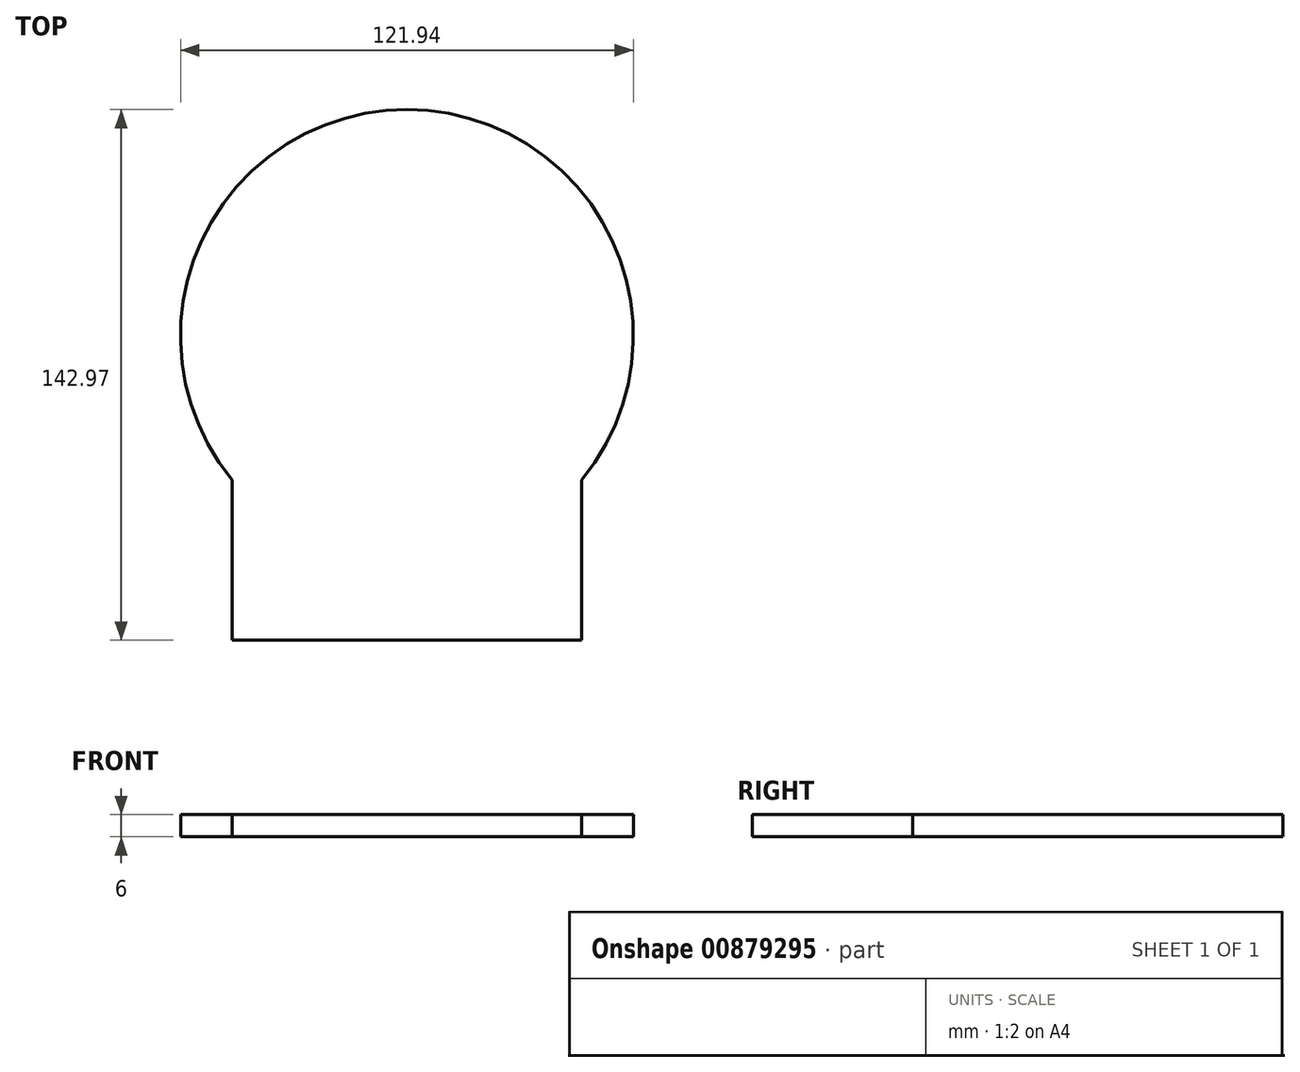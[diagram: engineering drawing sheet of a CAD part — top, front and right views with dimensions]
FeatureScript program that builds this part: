
annotation { "Feature Type Name" : "Feature", "Feature Type Description" : "" }
export const myFeature = defineFeature(function(context is Context, id is Id, definition is map)
    precondition{}
    {
        {
            var Q0;
            Q0=qCreatedBy(makeId("Top.planeOp"),FACE);
            var sketch = newSketch(context, id + "F0", { "sketchPlane" : qUnion([Q0])});
            skArc(sketch, "E0.0", {"start": v(-100, 44.36) * mm, "mid": v(-50, 149.43) * mm, "end": v(0, 44.36) * mm});
            skLineSegment(sketch, "E1.0", {"start": v(-100, 44.36) * mm, "end": v(-100, 0) * mm});
            skLineSegment(sketch, "E2.0", {"start": v(-100, 0) * mm, "end": v(0, 0) * mm});
            skLineSegment(sketch, "E3.0", {"start": v(0, 44.36) * mm, "end": v(0, 0) * mm});
            skLineSegment(sketch, "E4.0", {"start": v(-3, 46.16) * mm, "end": v(-3, 3) * mm});
            skArc(sketch, "E5.0", {"start": v(-97, 46.16) * mm, "mid": v(-50, 145.97) * mm, "end": v(-3, 46.16) * mm});
            skLineSegment(sketch, "E6.0", {"start": v(-97, 46.16) * mm, "end": v(-97, 3) * mm});
            skLineSegment(sketch, "E7.0", {"start": v(-97, 3) * mm, "end": v(-3, 3) * mm});
            skSolve(sketch);
        }
        {
            var Q0;
            Q0=makeQuery(id+"F0.imprint","IMPRINT",FACE,{"disambiguationData":[TD([[makeQuery(id+"F0.imprint","IMPRINT",EDGE,{"derivedFrom":sQuery(id+"F0.wireOp",EDGE,"E4.0")}),-1.0]])]});
            var Q1;
            Q1=makeQuery(id+"F0.imprint","IMPRINT",FACE,{"disambiguationData":[TD([[makeQuery(id+"F0.imprint","IMPRINT",EDGE,{"derivedFrom":sQuery(id+"F0.wireOp",EDGE,"E0.0")}),-1.0]])]});
            extrude(context, id + "F1", {"entities" : qUnion([Q0, Q1]), "depth" : 3 * mm, "offsetDistance" : 25 * mm});
        }
        {
            var Q0;
            Q0=makeQuery(id+"F0.imprint","IMPRINT",FACE,{"disambiguationData":[TD([[makeQuery(id+"F0.imprint","IMPRINT",EDGE,{"derivedFrom":sQuery(id+"F0.wireOp",EDGE,"E4.0")}),-1.0]])]});
            extrude(context, id + "F2", {"entities" : qUnion([Q0]), "operationType" : NewBodyOperationType.ADD, "oppositeDirection" : true, "depth" : 3 * mm, "offsetDistance" : 25 * mm});
        }
    });
